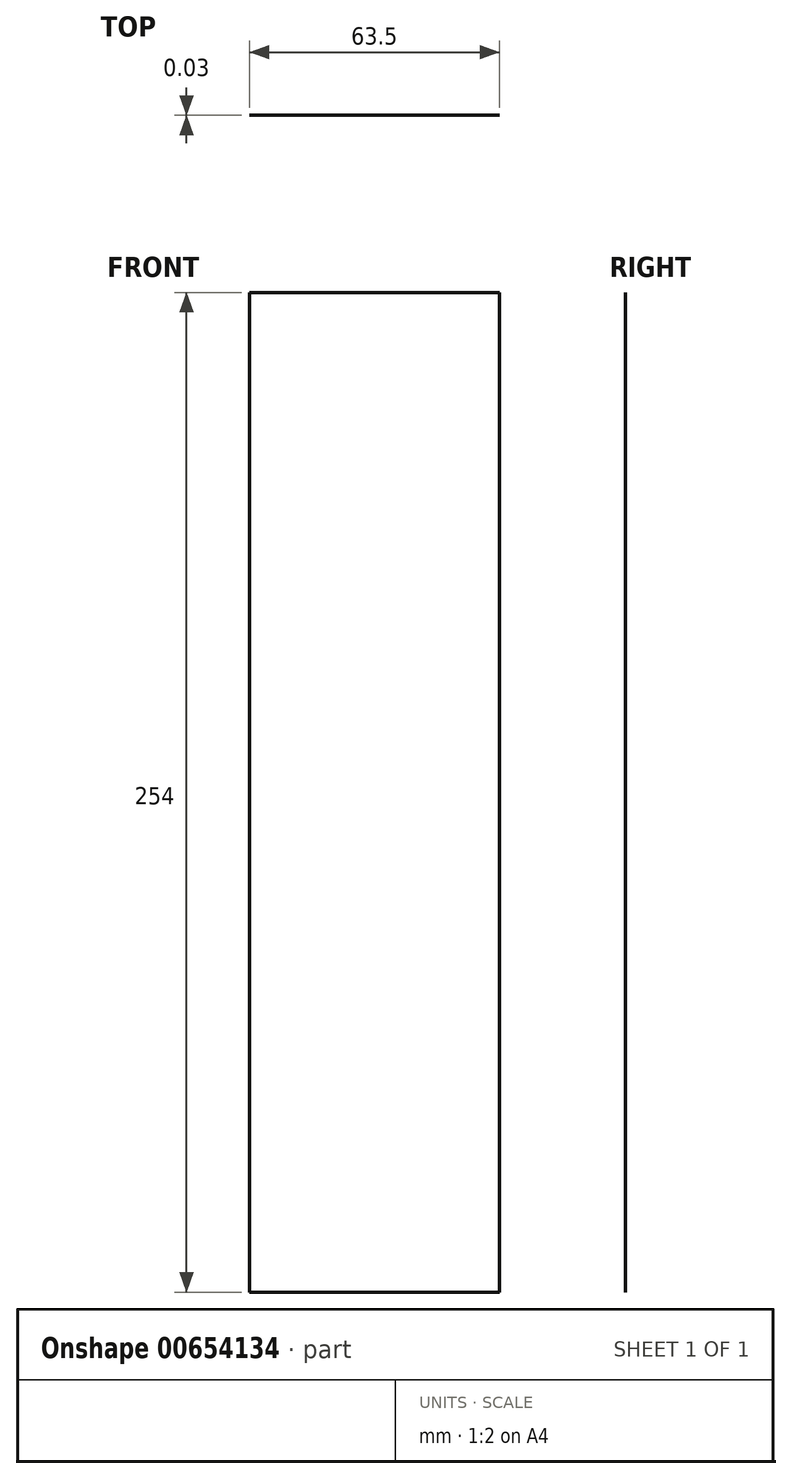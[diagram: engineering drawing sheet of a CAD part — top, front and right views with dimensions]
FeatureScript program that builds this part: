
annotation { "Feature Type Name" : "Feature", "Feature Type Description" : "" }
export const myFeature = defineFeature(function(context is Context, id is Id, definition is map)
    precondition{}
    {
        {
            var Q0;
            Q0=qCreatedBy(makeId("Front.planeOp"),FACE);
            var sketch = newSketch(context, id + "F0", { "sketchPlane" : qUnion([Q0])});
            skLineSegment(sketch, "E0.bottom", {"start": v(-31.75, 127) * mm, "end": v(31.75, 127) * mm});
            skLineSegment(sketch, "E0.top", {"start": v(-31.75, -127) * mm, "end": v(31.75, -127) * mm});
            skLineSegment(sketch, "E0.left", {"start": v(-31.75, 127) * mm, "end": v(-31.75, -127) * mm});
            skLineSegment(sketch, "E0.right", {"start": v(31.75, 127) * mm, "end": v(31.75, -127) * mm});
            skPoint(sketch, "E0.middle", {"position": v(0, 0) * mm});
            skSolve(sketch);
        }
        {
            var Q0;
            Q0=qSketchRegion(id+"F0",true);
            extrude(context, id + "F1", {"entities" : qUnion([Q0]), "depth" : 3 / 101.6 * mm, "offsetDistance" : 25.4 * mm});
        }
    });
